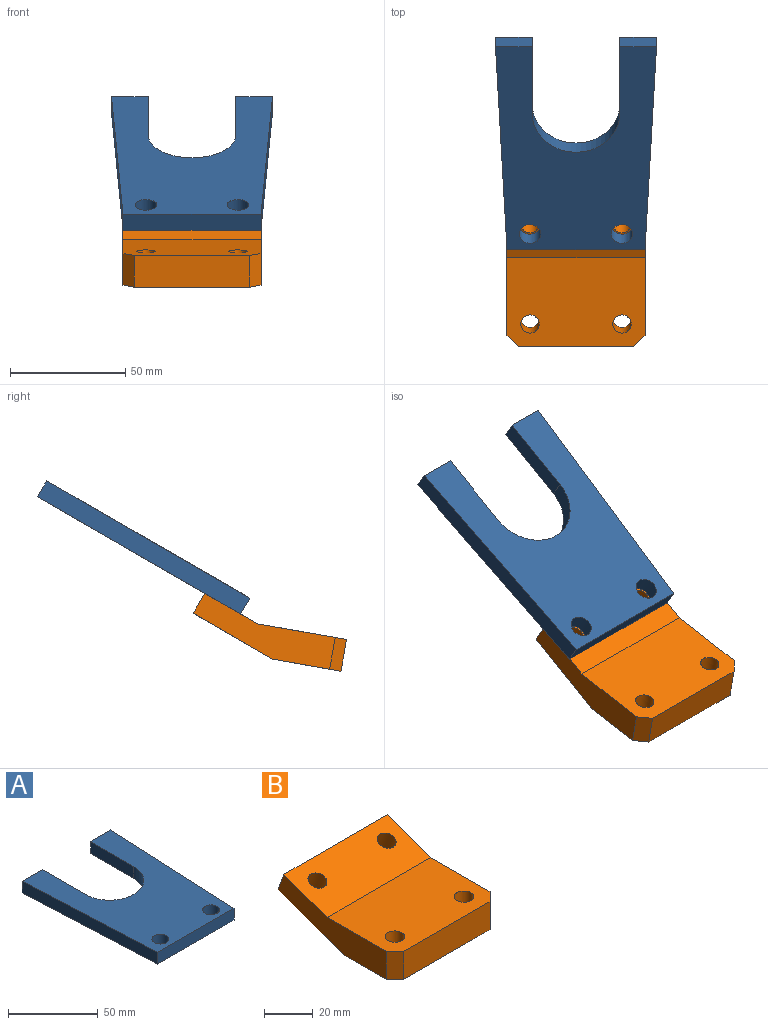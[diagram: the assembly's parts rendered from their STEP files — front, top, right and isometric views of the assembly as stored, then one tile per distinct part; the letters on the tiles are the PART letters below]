
ASSEMBLY  parts=2 mates=1
PART A: 12 faces, bbox 70x102x8 mm
  f0: plane 34x8mm, normal (1,0,0), area 272mm2, adj f1,f7,f10,f11
  f1: plane 16x8mm, normal (0,1,0), area 128mm2, adj f0,f2,f10,f11
  f2: plane 102x8mm, normal (-1,-0.05,0), area 817mm2, adj f1,f3,f10,f11
  f3: plane 60x8mm, normal (0,-1,0), area 480mm2, adj f2,f4,f10,f11
  f4: plane 102x8mm, normal (1,-0.05,0), area 817mm2, adj f3,f5,f10,f11
  f5: plane 16x8mm, normal (0,1,0), area 128mm2, adj f4,f6,f10,f11
  f6: plane 34x8mm, normal (-1,0,0), area 272mm2, adj f5,f7,f10,f11
  f7: cylinder r=19mm len=38mm, axis (0,0,-1), area 477.5mm2, adj f0,f6,f10,f11
  f8: cylinder r=4.7mm len=9.41mm, axis (0,0,-1), area 236.4mm2, adj f10,f11
  f9: cylinder r=4.7mm len=9.41mm, axis (0,0,-1), area 236.4mm2, adj f10,f11
  f10: plane 102x70mm, normal (0,0,1), area 4632mm2, adj f0,f1,f2,f3,f4,f5,f6,f7
  f11: plane 102x70mm, normal (0,0,-1), area 4632mm2, adj f0,f1,f2,f3,f4,f5,f6,f7
PART B: 14 faces, bbox 60x67.6x23.1 mm
  f0: plane 60x30mm, normal (0,0,-1), area 1674.5mm2, adj f1,f5,f6,f7,f8,f9,f12,f13
  f1: plane 60x37.59mm, normal (0,0.34,-0.94), area 2299.5mm2, adj f0,f2,f6,f7,f10,f11
  f2: plane 60x9.4mm, normal (0,0.94,0.34), area 600mm2, adj f1,f3,f6,f7
  f3: plane 60x24.94mm, normal (0,-0.34,0.94), area 1492mm2, adj f2,f4,f6,f7,f10,f11
  f4: plane 60x39.23mm, normal (0,0,1), area 2228.1mm2, adj f3,f5,f6,f7,f8,f9,f12,f13
  f5: plane 50x14mm, normal (0,-1,0), area 700mm2, adj f0,f4,f12,f13
  f6: plane 62.59x23.08mm, normal (1,0,0), area 747.3mm2, adj f0,f1,f2,f3,f4,f13
  f7: plane 62.59x23.08mm, normal (-1,0,0), area 747.3mm2, adj f0,f1,f2,f3,f4,f12
  f8: cylinder r=4mm len=14mm, axis (0,0,1), area 351.9mm2, adj f0,f4
  f9: cylinder r=4mm len=14mm, axis (0,0,1), area 351.9mm2, adj f0,f4
  f10: cylinder r=4mm len=12.13mm, axis (0,-0.34,0.94), area 251.3mm2, adj f1,f3
  f11: cylinder r=4mm len=12.13mm, axis (0,-0.34,0.94), area 251.3mm2, adj f1,f3
  f12: plane 14x5mm, normal (-0.71,-0.71,0), area 99mm2, adj f0,f4,f5,f7
  f13: plane 14x5mm, normal (0.71,-0.71,0), area 99mm2, adj f0,f4,f5,f6
PLACE A rot(axis=(0,-0.97,-0.26),180deg) t=(52.76,-115.85,-43.07)mm
PLACE B rot(axis=(1,0,0),10deg) t=(22.76,11.82,21.71)mm
MATE fastened A.f8 <-> B.f11  axis (0,0.5,-0.87) through (72.76,62.35,50.58)mm
